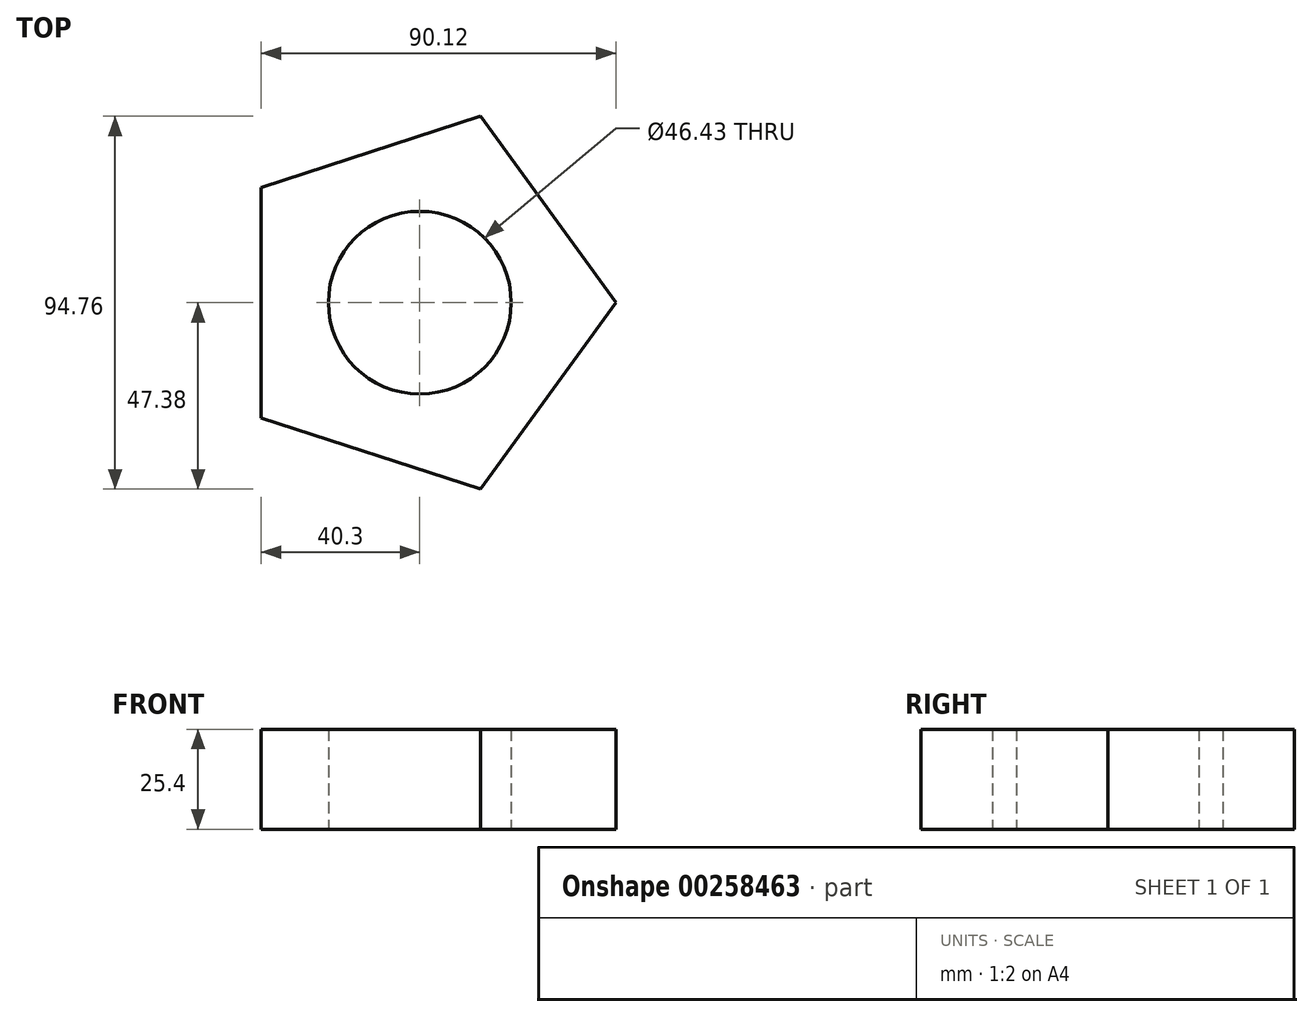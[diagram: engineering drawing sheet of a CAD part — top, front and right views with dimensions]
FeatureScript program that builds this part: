
annotation { "Feature Type Name" : "Feature", "Feature Type Description" : "" }
export const myFeature = defineFeature(function(context is Context, id is Id, definition is map)
    precondition{}
    {
        {
            var Q0;
            Q0=qCreatedBy(makeId("Top.planeOp"),FACE);
            var sketch = newSketch(context, id + "F0", { "sketchPlane" : qUnion([Q0])});
            skCircle(sketch, "E0.cCircle", {"center": v(0, 0) * mm, "radius": 40.3 * mm, "construction": true});
            skLineSegment(sketch, "E0.0", {"start": v(-40.3, -29.28) * mm, "end": v(-40.3, 29.28) * mm});
            skLineSegment(sketch, "E0.1", {"start": v(-40.3, 29.28) * mm, "end": v(15.4, 47.38) * mm});
            skLineSegment(sketch, "E0.2", {"start": v(15.4, 47.38) * mm, "end": v(49.82, 0) * mm});
            skLineSegment(sketch, "E0.3", {"start": v(49.82, 0) * mm, "end": v(15.4, -47.38) * mm});
            skLineSegment(sketch, "E0.4", {"start": v(15.4, -47.38) * mm, "end": v(-40.3, -29.28) * mm});
            skPoint(sketch, "E0.0.midPoint", {"position": v(-40.3, 0) * mm});
            skCircle(sketch, "E1", {"center": v(0, 0) * mm, "radius": 23.21 * mm});
            skSolve(sketch);
        }
        {
            var Q0;
            Q0=makeQuery(id+"F0.imprint","IMPRINT",FACE,{"disambiguationData":[TD([[makeQuery(id+"F0.imprint","IMPRINT",EDGE,{"derivedFrom":sQuery(id+"F0.wireOp",EDGE,"E0.0")}),-1.0]])]});
            extrude(context, id + "F1", {"entities" : qUnion([Q0]), "depth" : 25.4 * mm});
        }
    });
